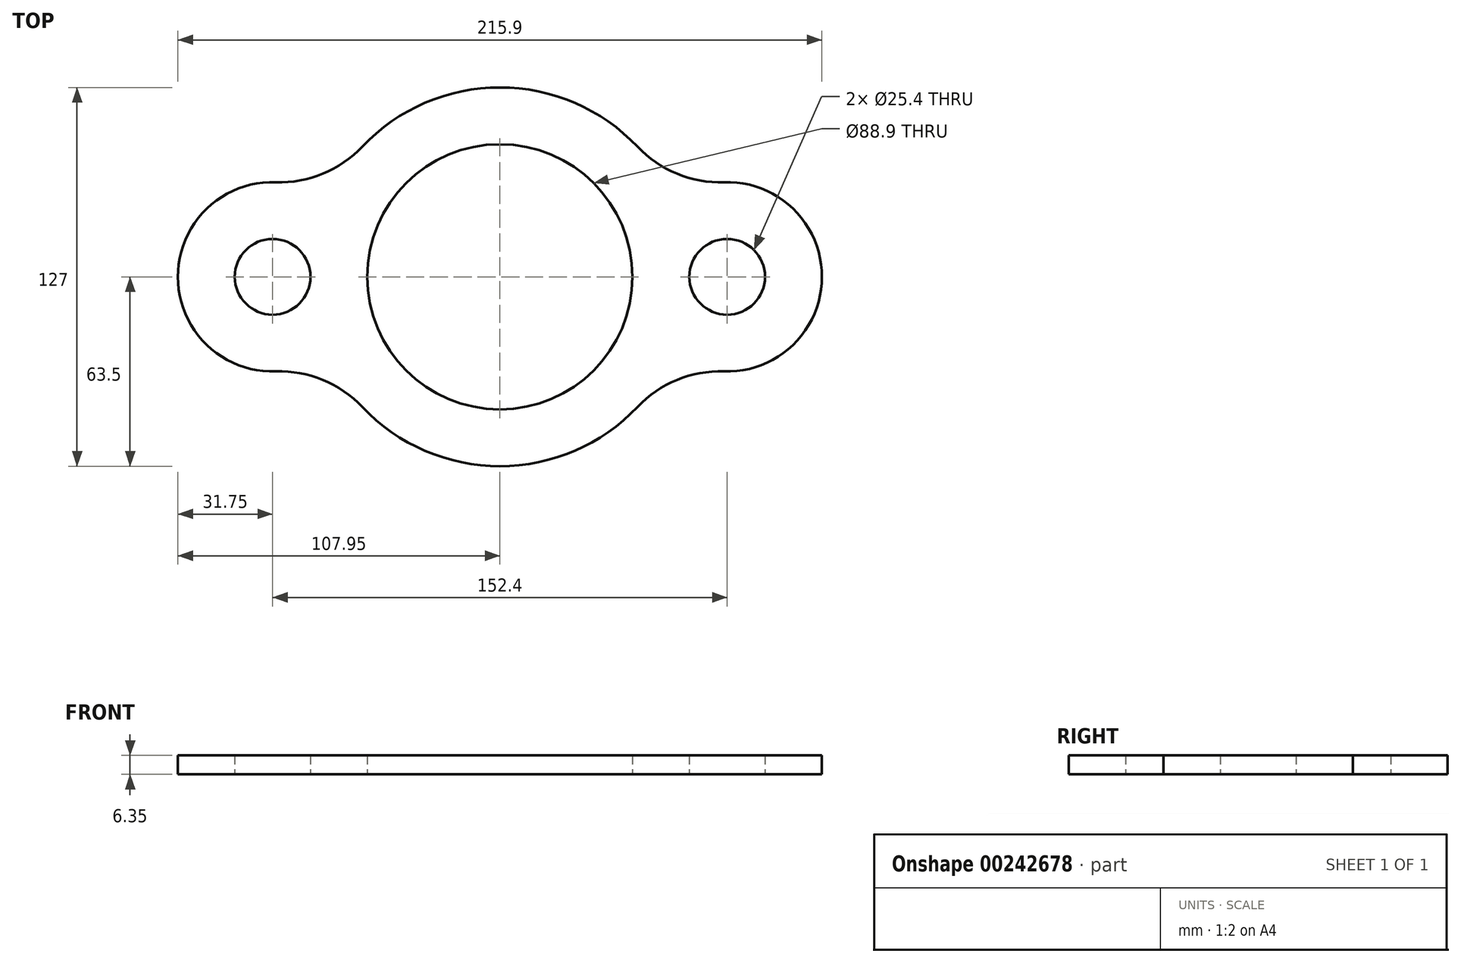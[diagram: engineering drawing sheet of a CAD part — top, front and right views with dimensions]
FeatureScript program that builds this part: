
annotation { "Feature Type Name" : "Feature", "Feature Type Description" : "" }
export const myFeature = defineFeature(function(context is Context, id is Id, definition is map)
    precondition{}
    {
        {
            var Q0;
            Q0=qCreatedBy(makeId("Top.planeOp"),FACE);
            var sketch = newSketch(context, id + "F0", { "sketchPlane" : qUnion([Q0])});
            skArc(sketch, "E0", {"start": v(-46.14, -43.63) * mm, "mid": v(0, -63.5) * mm, "end": v(46.14, -43.63) * mm});
            skCircle(sketch, "E1", {"center": v(0, 0) * mm, "radius": 44.45 * mm});
            skArc(sketch, "E2", {"start": v(-75.12, 31.73) * mm, "mid": v(-107.95, 0) * mm, "end": v(-75.12, -31.73) * mm});
            skCircle(sketch, "E3", {"center": v(-76.2, 0) * mm, "radius": 12.7 * mm});
            skArc(sketch, "E4", {"start": v(75.12, -31.73) * mm, "mid": v(107.95, 0) * mm, "end": v(75.12, 31.73) * mm});
            skCircle(sketch, "E5", {"center": v(76.2, 0) * mm, "radius": 12.7 * mm});
            skArc(sketch, "E6.trimOffspring", {"start": v(46.14, 43.63) * mm, "mid": v(0, 63.5) * mm, "end": v(-46.14, 43.63) * mm});
            skPoint(sketch, "E7.visualSharp", {"position": v(-57.94, -25.98) * mm});
            skArc(sketch, "E7.filletArc", {"start": v(-46.14, -43.63) * mm, "mid": v(-59.35, -34.56) * mm, "end": v(-75.12, -31.73) * mm});
            skPoint(sketch, "E8.visualSharp", {"position": v(-57.94, 25.98) * mm});
            skArc(sketch, "E8.filletArc", {"start": v(-75.12, 31.73) * mm, "mid": v(-59.35, 34.56) * mm, "end": v(-46.14, 43.63) * mm});
            skPoint(sketch, "E9.visualSharp", {"position": v(57.94, 25.98) * mm});
            skArc(sketch, "E9.filletArc", {"start": v(46.14, 43.63) * mm, "mid": v(59.35, 34.56) * mm, "end": v(75.12, 31.73) * mm});
            skPoint(sketch, "E10.visualSharp", {"position": v(57.94, -25.98) * mm});
            skArc(sketch, "E10.filletArc", {"start": v(75.12, -31.73) * mm, "mid": v(59.35, -34.56) * mm, "end": v(46.14, -43.63) * mm});
            skSolve(sketch);
        }
        {
            var Q0;
            Q0=makeQuery(id+"F0.imprint","IMPRINT",FACE,{"disambiguationData":[TD([[makeQuery(id+"F0.imprint","IMPRINT",EDGE,{"derivedFrom":sQuery(id+"F0.wireOp",EDGE,"E0")}),1.0]])]});
            extrude(context, id + "F1", {"entities" : qUnion([Q0]), "depth" : 6.35 * mm});
        }
    });
